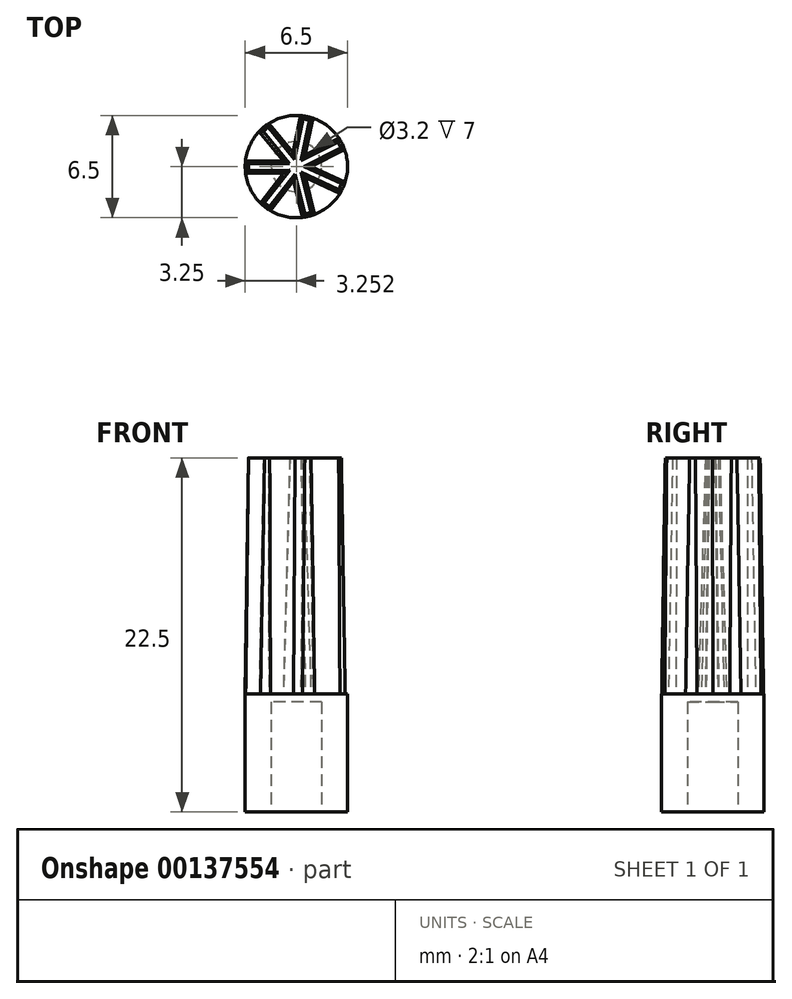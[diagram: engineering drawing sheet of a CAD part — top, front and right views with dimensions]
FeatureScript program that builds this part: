
annotation { "Feature Type Name" : "Feature", "Feature Type Description" : "" }
export const myFeature = defineFeature(function(context is Context, id is Id, definition is map)
    precondition{}
    {
        {
            var Q0;
            Q0=qCreatedBy(makeId("Top.planeOp"),FACE);
            var sketch = newSketch(context, id + "F0", { "sketchPlane" : qUnion([Q0])});
            skCircle(sketch, "E0", {"center": v(-17.52, 0) * mm, "radius": 3.25 * mm});
            skCircle(sketch, "E1", {"center": v(-17.52, 0) * mm, "radius": 1.6 * mm});
            skSolve(sketch);
        }
        {
            var Q0;
            Q0=makeQuery(id+"F0.imprint","IMPRINT",FACE,{"disambiguationData":[TD([[makeQuery(id+"F0.imprint","IMPRINT",EDGE,{"derivedFrom":sQuery(id+"F0.wireOp",EDGE,"E0")}),1.0]])]});
            var Q1;
            Q1=makeQuery(id+"F0.imprint","IMPRINT",FACE,{"disambiguationData":[TD([[makeQuery(id+"F0.imprint","IMPRINT",EDGE,{"derivedFrom":sQuery(id+"F0.wireOp",EDGE,"E1")}),1.0]])]});
            extrude(context, id + "F1", {"entities" : qUnion([Q0, Q1]), "depth" : 7.5 * mm});
        }
        {
            var Q0;
            Q0=makeQuery(id+"F1.opExtrude","CAP_FACE",FACE,{"disambiguationData":[OSD([sQuery(id+"F0.wireOp",EDGE,"E0")])],"isStart":false});
            var sketch = newSketch(context, id + "F2", { "sketchPlane" : qUnion([Q0])});
            skPoint(sketch, "E2.center", {"position": v(-17.52, 0) * mm});
            skLineSegment(sketch, "E3", {"start": v(-17.52, 0) * mm, "end": v(-20.77, -0.06) * mm});
            skLineSegment(sketch, "E4", {"start": v(-17.53, 0.4) * mm, "end": v(-20.75, 0.34) * mm});
            skLineSegment(sketch, "E5", {"start": v(-20.74, -0.46) * mm, "end": v(-17.51, -0.4) * mm});
            skLineSegment(sketch, "E6", {"start": v(-17.53, 0.4) * mm, "end": v(-17.52, 0) * mm});
            skLineSegment(sketch, "E7", {"start": v(-17.52, 0) * mm, "end": v(-17.51, -0.4) * mm});
            skLineSegment(sketch, "E8.1.0", {"start": v(-17.84, 0.24) * mm, "end": v(-19.8, -2.31) * mm});
            skLineSegment(sketch, "E8.1.1", {"start": v(-19.17, -2.8) * mm, "end": v(-17.2, -0.24) * mm});
            skLineSegment(sketch, "E8.2.0", {"start": v(-17.9, -0.1) * mm, "end": v(-17.13, -3.23) * mm});
            skLineSegment(sketch, "E8.2.1", {"start": v(-16.35, -3.03) * mm, "end": v(-17.13, 0.1) * mm});
            skLineSegment(sketch, "E8.3.0", {"start": v(-17.68, -0.36) * mm, "end": v(-14.75, -1.7) * mm});
            skLineSegment(sketch, "E8.3.1", {"start": v(-14.42, -0.98) * mm, "end": v(-17.35, 0.36) * mm});
            skLineSegment(sketch, "E8.4.0", {"start": v(-17.34, -0.36) * mm, "end": v(-14.46, 1.1) * mm});
            skLineSegment(sketch, "E8.4.1", {"start": v(-14.82, 1.8) * mm, "end": v(-17.7, 0.36) * mm});
            skLineSegment(sketch, "E8.5.0", {"start": v(-17.13, -0.08) * mm, "end": v(-16.47, 3.07) * mm});
            skLineSegment(sketch, "E8.5.1", {"start": v(-17.25, 3.24) * mm, "end": v(-17.9, 0.08) * mm});
            skLineSegment(sketch, "E8.6.0", {"start": v(-17.2, 0.26) * mm, "end": v(-19.27, 2.74) * mm});
            skLineSegment(sketch, "E8.6.1", {"start": v(-19.88, 2.23) * mm, "end": v(-17.83, -0.26) * mm});
            skSolve(sketch);
        }
        {
            var Q0;
            Q0=makeQuery(id+"F0.imprint","IMPRINT",FACE,{"disambiguationData":[TD([[makeQuery(id+"F0.imprint","IMPRINT",EDGE,{"derivedFrom":sQuery(id+"F0.wireOp",EDGE,"E1")}),1.0]])]});
            var Q1;
            Q1=makeQuery(id+"F1.opExtrude","CAP_FACE",FACE,{"disambiguationData":[OSD([sQuery(id+"F0.wireOp",EDGE,"E0")])],"isStart":false});
            extrude(context, id + "F3", {"entities" : qUnion([Q0]), "operationType" : NewBodyOperationType.REMOVE, "endBoundEntityFace" : qUnion([Q1]), "depth" : 7 * mm});
        }
        {
            var Q0;
            {var subQ4=sQuery(id+"F2.wireOp",EDGE,"E6");Q0=makeQuery(id+"F2.imprint","IMPRINT",FACE,{"disambiguationData":[TD([[makeQuery(id+"F2.imprint","IMPRINT",EDGE,{"derivedFrom":subQ4}),-1.0]])]});}
            var Q1;
            {var subQ19=sQuery(id+"F2.wireOp",EDGE,"E6");Q1=makeQuery(id+"F2.imprint","IMPRINT",FACE,{"disambiguationData":[TD([[makeQuery(id+"F2.imprint","IMPRINT",EDGE,{"derivedFrom":subQ19}),1.0]])]});}
            var Q2;
            {var subQ0=sQuery(id+"F2.wireOp",EDGE,"E7");Q2=makeQuery(id+"F2.imprint","IMPRINT",FACE,{"disambiguationData":[TD([[makeQuery(id+"F2.imprint","IMPRINT",EDGE,{"derivedFrom":subQ0}),-1.0]])]});}
            var Q3;
            {var subQ0=sQuery(id+"F2.wireOp",EDGE,"E8.3.0");var subQ1=sQuery(id+"F2.wireOp",EDGE,"E5");var subQ2=makeQuery(id+"F2.imprint","INTERSECT",VERTEX,{"derivedFrom":[subQ1,subQ0]});Q3=makeQuery(id+"F2.imprint","IMPRINT",FACE,{"disambiguationData":[TD([[makeQuery(id+"F2.imprint","IMPRINT",EDGE,{"disambiguationData":[TD([[subQ2,1.0]])],"derivedFrom":subQ1}),-1.0]])]});}
            var Q4;
            {var subQ0=sQuery(id+"F2.wireOp",EDGE,"E8.4.0");var subQ1=sQuery(id+"F2.wireOp",EDGE,"E8.1.1");var subQ2=makeQuery(id+"F2.imprint","INTERSECT",VERTEX,{"derivedFrom":[subQ1,subQ0]});Q4=makeQuery(id+"F2.imprint","IMPRINT",FACE,{"disambiguationData":[TD([[makeQuery(id+"F2.imprint","IMPRINT",EDGE,{"disambiguationData":[TD([[subQ2,1.0]])],"derivedFrom":subQ1}),-1.0]])]});}
            var Q5;
            {var subQ0=sQuery(id+"F2.wireOp",EDGE,"E8.5.0");var subQ1=sQuery(id+"F2.wireOp",EDGE,"E8.2.1");var subQ2=makeQuery(id+"F2.imprint","INTERSECT",VERTEX,{"derivedFrom":[subQ1,subQ0]});Q5=makeQuery(id+"F2.imprint","IMPRINT",FACE,{"disambiguationData":[TD([[makeQuery(id+"F2.imprint","IMPRINT",EDGE,{"disambiguationData":[TD([[subQ2,1.0]])],"derivedFrom":subQ1}),-1.0]])]});}
            var Q6;
            {var subQ0=sQuery(id+"F2.wireOp",EDGE,"E8.6.0");var subQ1=sQuery(id+"F2.wireOp",EDGE,"E8.3.1");var subQ2=makeQuery(id+"F2.imprint","INTERSECT",VERTEX,{"derivedFrom":[subQ1,subQ0]});Q6=makeQuery(id+"F2.imprint","IMPRINT",FACE,{"disambiguationData":[TD([[makeQuery(id+"F2.imprint","IMPRINT",EDGE,{"disambiguationData":[TD([[subQ2,1.0]])],"derivedFrom":subQ1}),-1.0]])]});}
            var Q7;
            {var subQ0=sQuery(id+"F2.wireOp",EDGE,"E8.4.1");var subQ1=sQuery(id+"F2.wireOp",EDGE,"E4");var subQ2=makeQuery(id+"F2.imprint","INTERSECT",VERTEX,{"derivedFrom":[subQ1,subQ0]});Q7=makeQuery(id+"F2.imprint","IMPRINT",FACE,{"disambiguationData":[TD([[makeQuery(id+"F2.imprint","IMPRINT",EDGE,{"disambiguationData":[TD([[subQ2,-1.0]])],"derivedFrom":subQ1}),-1.0]])]});}
            var Q8;
            {var subQ0=sQuery(id+"F2.wireOp",EDGE,"E8.5.1");var subQ1=sQuery(id+"F2.wireOp",EDGE,"E4");var subQ2=makeQuery(id+"F2.imprint","INTERSECT",VERTEX,{"derivedFrom":[subQ1,subQ0]});Q8=makeQuery(id+"F2.imprint","IMPRINT",FACE,{"disambiguationData":[TD([[makeQuery(id+"F2.imprint","IMPRINT",EDGE,{"disambiguationData":[TD([[subQ2,-1.0]])],"derivedFrom":subQ1}),1.0]])]});}
            var Q9;
            {var subQ0=sQuery(id+"F2.wireOp",EDGE,"E8.1.0");var subQ1=sQuery(id+"F2.wireOp",EDGE,"E5");var subQ2=makeQuery(id+"F2.imprint","INTERSECT",VERTEX,{"derivedFrom":[subQ1,subQ0]});Q9=makeQuery(id+"F2.imprint","IMPRINT",FACE,{"disambiguationData":[TD([[makeQuery(id+"F2.imprint","IMPRINT",EDGE,{"disambiguationData":[TD([[subQ2,-1.0]])],"derivedFrom":subQ1}),1.0]])]});}
            var Q10;
            {var subQ1=sQuery(id+"F2.wireOp",EDGE,"E8.1.1");var subQ5=sQuery(id+"F2.wireOp",EDGE,"E8.2.0");var subQ8=makeQuery(id+"F2.imprint","INTERSECT",VERTEX,{"derivedFrom":[subQ1,subQ5]});Q10=makeQuery(id+"F2.imprint","IMPRINT",FACE,{"disambiguationData":[TD([[makeQuery(id+"F2.imprint","IMPRINT",EDGE,{"disambiguationData":[TD([[subQ8,-1.0]])],"derivedFrom":subQ1}),-1.0]])]});}
            var Q11;
            {var subQ5=sQuery(id+"F2.wireOp",EDGE,"E5");var subQ7=sQuery(id+"F2.wireOp",EDGE,"E8.1.0");var subQ9=makeQuery(id+"F2.imprint","INTERSECT",VERTEX,{"derivedFrom":[subQ5,subQ7]});Q11=makeQuery(id+"F2.imprint","IMPRINT",FACE,{"disambiguationData":[TD([[makeQuery(id+"F2.imprint","IMPRINT",EDGE,{"disambiguationData":[TD([[subQ9,-1.0]])],"derivedFrom":subQ5}),-1.0]])]});}
            var Q12;
            {var subQ1=sQuery(id+"F2.wireOp",EDGE,"E8.2.1");var subQ5=sQuery(id+"F2.wireOp",EDGE,"E8.3.0");var subQ8=makeQuery(id+"F2.imprint","INTERSECT",VERTEX,{"derivedFrom":[subQ1,subQ5]});Q12=makeQuery(id+"F2.imprint","IMPRINT",FACE,{"disambiguationData":[TD([[makeQuery(id+"F2.imprint","IMPRINT",EDGE,{"disambiguationData":[TD([[subQ8,-1.0]])],"derivedFrom":subQ1}),-1.0]])]});}
            var Q13;
            {var subQ1=makeQuery(id+"F1.opExtrude","CAP_EDGE",EDGE,{"disambiguationData":[OSD([sQuery(id+"F0.wireOp",EDGE,"E0")])],"isStart":false});var subQ5=sQuery(id+"F2.wireOp",EDGE,"E4");var subQ7=makeQuery(id+"F2.imprint","INTERSECT",VERTEX,{"derivedFrom":[subQ1,subQ5]});Q13=makeQuery(id+"F2.imprint","IMPRINT",FACE,{"disambiguationData":[TD([[makeQuery(id+"F2.imprint","IMPRINT",EDGE,{"disambiguationData":[TD([[subQ7,1.0]])],"derivedFrom":subQ5}),1.0]])]});}
            var Q14;
            {var subQ1=makeQuery(id+"F1.opExtrude","CAP_EDGE",EDGE,{"disambiguationData":[OSD([sQuery(id+"F0.wireOp",EDGE,"E0")])],"isStart":false});var subQ5=sQuery(id+"F2.wireOp",EDGE,"E5");var subQ6=makeQuery(id+"F2.imprint","INTERSECT",VERTEX,{"derivedFrom":[subQ1,subQ5]});Q14=makeQuery(id+"F2.imprint","IMPRINT",FACE,{"disambiguationData":[TD([[makeQuery(id+"F2.imprint","IMPRINT",EDGE,{"disambiguationData":[TD([[subQ6,-1.0]])],"derivedFrom":subQ5}),1.0]])]});}
            var Q15;
            {var subQ1=sQuery(id+"F2.wireOp",EDGE,"E8.3.1");var subQ5=sQuery(id+"F2.wireOp",EDGE,"E8.4.0");var subQ8=makeQuery(id+"F2.imprint","INTERSECT",VERTEX,{"derivedFrom":[subQ1,subQ5]});Q15=makeQuery(id+"F2.imprint","IMPRINT",FACE,{"disambiguationData":[TD([[makeQuery(id+"F2.imprint","IMPRINT",EDGE,{"disambiguationData":[TD([[subQ8,-1.0]])],"derivedFrom":subQ1}),-1.0]])]});}
            var Q16;
            {var subQ1=sQuery(id+"F2.wireOp",EDGE,"E8.4.1");var subQ5=sQuery(id+"F2.wireOp",EDGE,"E8.5.0");var subQ8=makeQuery(id+"F2.imprint","INTERSECT",VERTEX,{"derivedFrom":[subQ1,subQ5]});Q16=makeQuery(id+"F2.imprint","IMPRINT",FACE,{"disambiguationData":[TD([[makeQuery(id+"F2.imprint","IMPRINT",EDGE,{"disambiguationData":[TD([[subQ8,-1.0]])],"derivedFrom":subQ1}),-1.0]])]});}
            var Q17;
            {var subQ3=sQuery(id+"F2.wireOp",EDGE,"E4");var subQ5=sQuery(id+"F2.wireOp",EDGE,"E8.5.1");var subQ6=makeQuery(id+"F2.imprint","INTERSECT",VERTEX,{"derivedFrom":[subQ3,subQ5]});Q17=makeQuery(id+"F2.imprint","IMPRINT",FACE,{"disambiguationData":[TD([[makeQuery(id+"F2.imprint","IMPRINT",EDGE,{"disambiguationData":[TD([[subQ6,-1.0]])],"derivedFrom":subQ3}),-1.0]])]});}
            extrude(context, id + "F4", {"entities" : qUnion([Q0, Q1, Q2, Q3, Q4, Q5, Q6, Q7, Q8, Q9, Q10, Q11, Q12, Q13, Q14, Q15, Q16, Q17]), "operationType" : NewBodyOperationType.ADD, "depth" : 15 * mm, "hasDraft" : true, "draftAngle" : 0.75 * degree, "draftPullDirection" : true});
        }
        {
            var Q0;
            Q0=makeQuery(id+"F4.opExtrude","CAP_FACE",FACE,{"disambiguationData":[OSD([sQuery(id+"F0.wireOp",EDGE,"E0"),sQuery(id+"F2.wireOp",EDGE,"E4"),sQuery(id+"F2.wireOp",EDGE,"E5"),sQuery(id+"F2.wireOp",EDGE,"E8.1.0"),sQuery(id+"F2.wireOp",EDGE,"E8.1.1"),sQuery(id+"F2.wireOp",EDGE,"E8.2.0"),sQuery(id+"F2.wireOp",EDGE,"E8.2.1"),sQuery(id+"F2.wireOp",EDGE,"E8.3.0"),sQuery(id+"F2.wireOp",EDGE,"E8.3.1"),sQuery(id+"F2.wireOp",EDGE,"E8.4.0"),sQuery(id+"F2.wireOp",EDGE,"E8.4.1"),sQuery(id+"F2.wireOp",EDGE,"E8.5.0"),sQuery(id+"F2.wireOp",EDGE,"E8.5.1"),sQuery(id+"F2.wireOp",EDGE,"E8.6.0"),sQuery(id+"F2.wireOp",EDGE,"E8.6.1")])],"isStart":false});
            var sketch = newSketch(context, id + "F5", { "sketchPlane" : qUnion([Q0])});
            skPoint(sketch, "E9", {"position": v(-17.36, 0) * mm});
            skPoint(sketch, "E9.positionSnap0", {"position": v(-17.36, 1.74) * mm});
            skSolve(sketch);
        }
        {
            var Q0;
            Q0=makeQuery(id+"F4.opExtrude","CAP_EDGE",EDGE,{"disambiguationData":[OSD([sQuery(id+"F2.wireOp",EDGE,"E8.2.0")])],"isStart":false});
            cPlane(context, id + "F6", {"entities" : qUnion([Q0]), "cplaneType" : CPlaneType.LINE_ANGLE, "offset" : 5 * mm, "angle" : 90 * degree, "width" : 150 * mm, "height" : 150 * mm});
        }
    });
